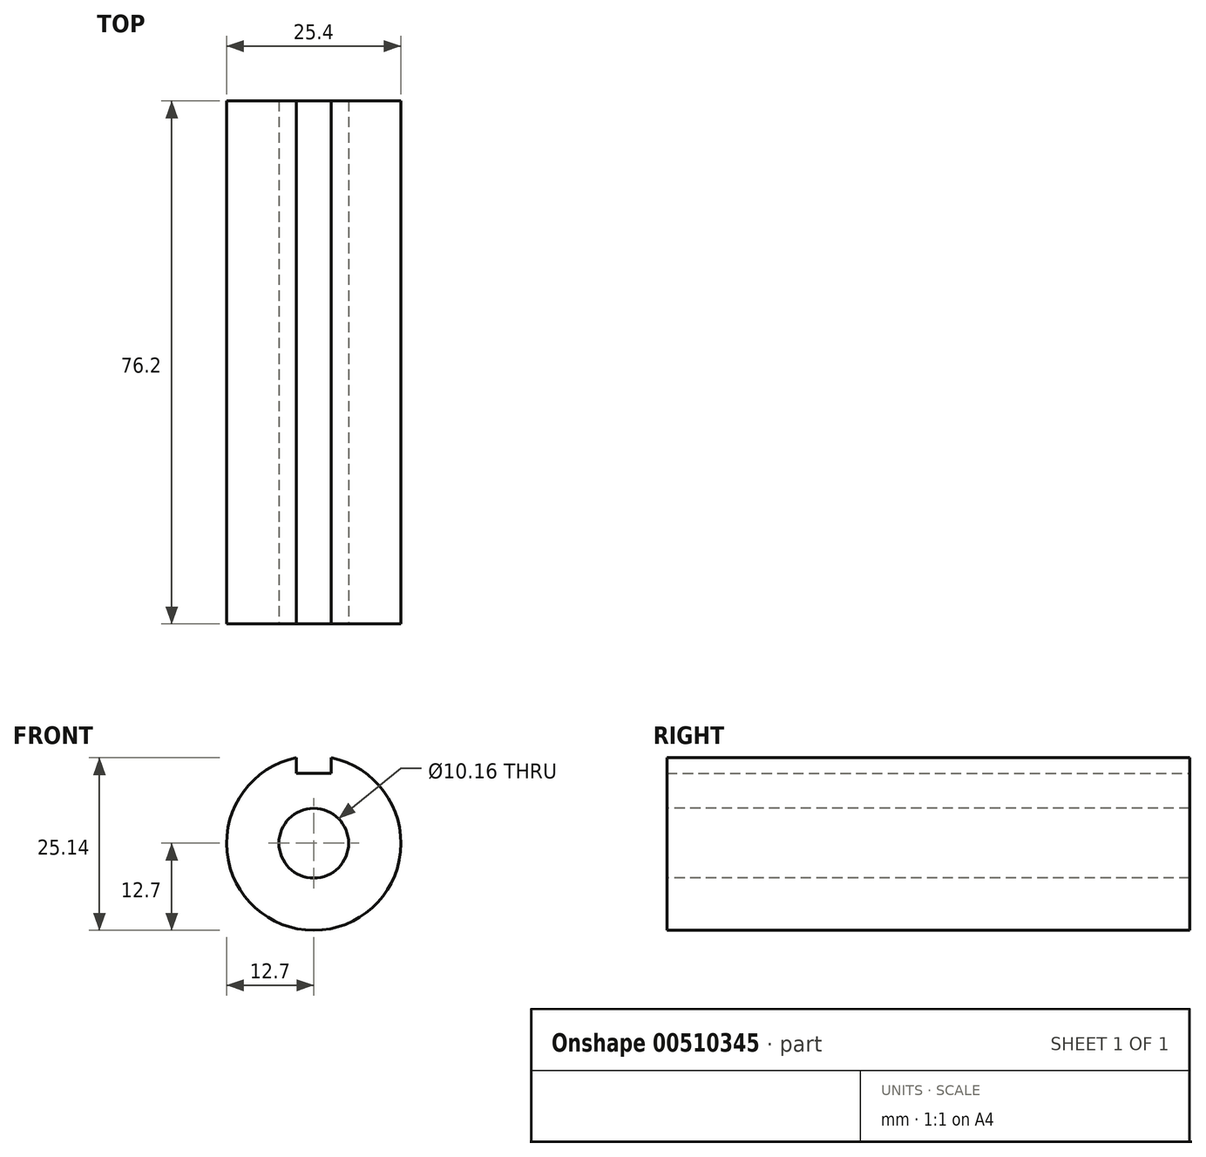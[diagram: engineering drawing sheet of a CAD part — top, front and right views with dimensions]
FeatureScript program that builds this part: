
annotation { "Feature Type Name" : "Feature", "Feature Type Description" : "" }
export const myFeature = defineFeature(function(context is Context, id is Id, definition is map)
    precondition{}
    {
        {
            var Q0;
            Q0=qCreatedBy(makeId("Front.planeOp"),FACE);
            var sketch = newSketch(context, id + "F0", { "sketchPlane" : qUnion([Q0])});
            skArc(sketch, "E0", {"start": v(-2.54, 12.44) * mm, "mid": v(0, -12.7) * mm, "end": v(2.54, 12.44) * mm});
            skLineSegment(sketch, "E1.top", {"start": v(-2.54, 10.16) * mm, "end": v(2.54, 10.16) * mm});
            skLineSegment(sketch, "E1.left", {"start": v(-2.54, 12.44) * mm, "end": v(-2.54, 10.16) * mm});
            skLineSegment(sketch, "E1.right", {"start": v(2.54, 12.44) * mm, "end": v(2.54, 10.16) * mm});
            skSolve(sketch);
        }
        {
            var Q0;
            Q0=makeQuery(id+"F0.imprint","IMPRINT",FACE,{"disambiguationData":[TD([[makeQuery(id+"F0.imprint","IMPRINT",EDGE,{"derivedFrom":sQuery(id+"F0.wireOp",EDGE,"E0")}),1.0]])]});
            extrude(context, id + "F1", {"entities" : qUnion([Q0]), "depth" : 76.2 * mm});
        }
        {
            var Q0;
            Q0=makeQuery(id+"F1.opExtrude","CAP_FACE",FACE,{"disambiguationData":[OSD([sQuery(id+"F0.wireOp",EDGE,"E0"),sQuery(id+"F0.wireOp",EDGE,"E1.top"),sQuery(id+"F0.wireOp",EDGE,"E1.left"),sQuery(id+"F0.wireOp",EDGE,"E1.right")])],"isStart":false});
            var sketch = newSketch(context, id + "F2", { "sketchPlane" : qUnion([Q0])});
            skCircle(sketch, "E2", {"center": v(0, 0) * mm, "radius": 5.08 * mm});
            skSolve(sketch);
        }
        {
            var Q0;
            Q0=makeQuery(id+"F2.imprint","IMPRINT",FACE,{"disambiguationData":[TD([[makeQuery(id+"F2.imprint","IMPRINT",EDGE,{"derivedFrom":sQuery(id+"F2.wireOp",EDGE,"E2")}),1.0]])]});
            extrude(context, id + "F3", {"entities" : qUnion([Q0]), "operationType" : NewBodyOperationType.REMOVE, "endBound" : BoundingType.UP_TO_NEXT, "oppositeDirection" : true, "depth" : 25.4 * mm});
        }
    });
